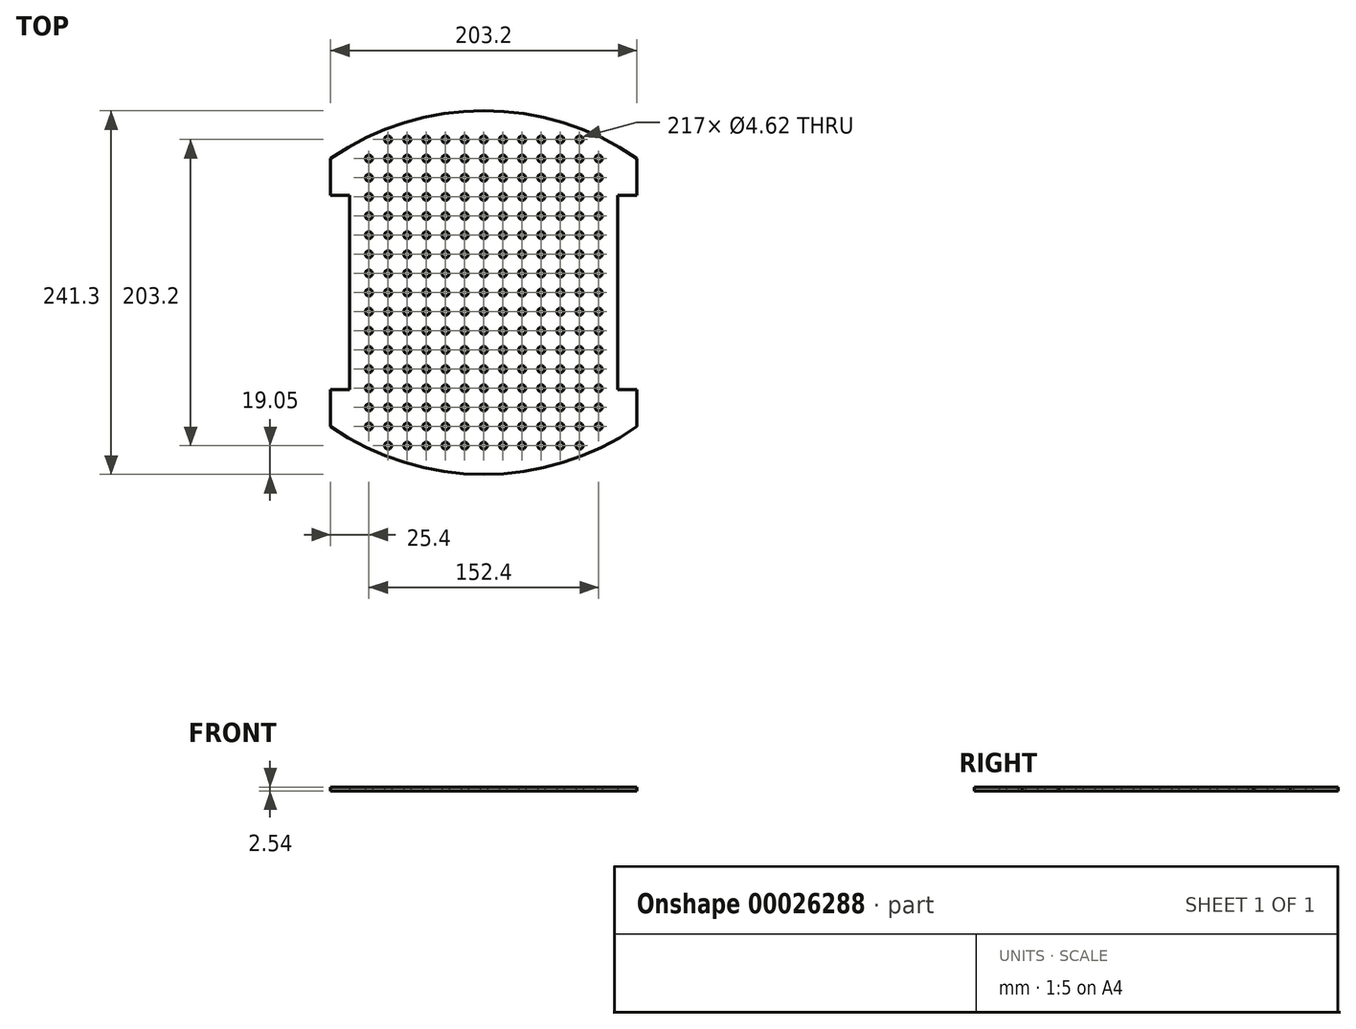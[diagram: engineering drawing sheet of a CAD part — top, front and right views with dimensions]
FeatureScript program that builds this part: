
annotation { "Feature Type Name" : "Feature", "Feature Type Description" : "" }
export const myFeature = defineFeature(function(context is Context, id is Id, definition is map)
    precondition{}
    {
        {
            var Q0;
            Q0=qCreatedBy(makeId("Top.planeOp"),FACE);
            var sketch = newSketch(context, id + "F0", { "sketchPlane" : qUnion([Q0])});
            skLineSegment(sketch, "E0", {"start": v(-101.6, 64.48) * mm, "end": v(-101.6, 88.9) * mm});
            skPoint(sketch, "E1.orphan", {"position": v(0, 120.65) * mm});
            skLineSegment(sketch, "E2.MirrorCS", {"start": v(-101.6, -88.9) * mm, "end": v(-101.6, -64.48) * mm});
            skLineSegment(sketch, "E3.MirrorCS", {"start": v(101.6, -88.9) * mm, "end": v(101.6, -64.48) * mm});
            skLineSegment(sketch, "E4.bottom", {"start": v(-101.6, 64.48) * mm, "end": v(-88.9, 64.48) * mm});
            skLineSegment(sketch, "E4.top", {"start": v(-101.6, -64.48) * mm, "end": v(-88.9, -64.48) * mm});
            skLineSegment(sketch, "E4.right", {"start": v(-88.9, 64.48) * mm, "end": v(-88.9, -64.48) * mm});
            skLineSegment(sketch, "E5.trimOffspring", {"start": v(-101.6, -64.48) * mm, "end": v(-101.6, -83.53) * mm});
            skLineSegment(sketch, "E6.MirrorCS", {"start": v(101.6, 64.48) * mm, "end": v(88.9, 64.48) * mm});
            skLineSegment(sketch, "E7.MirrorCS", {"start": v(88.9, 64.48) * mm, "end": v(88.9, -64.48) * mm});
            skLineSegment(sketch, "E8.MirrorCS", {"start": v(101.6, -64.48) * mm, "end": v(88.9, -64.48) * mm});
            skPoint(sketch, "E9.orphan", {"position": v(101.6, 64.48) * mm});
            skLineSegment(sketch, "E10", {"start": v(101.6, 88.9) * mm, "end": v(101.6, 64.48) * mm});
            skPoint(sketch, "E11.MirrorCS.end.orphan", {"position": v(0, -120.65) * mm});
            skLineSegment(sketch, "E12.trimOffspring", {"start": v(7.61, 0) * mm, "end": v(7.62, 0) * mm, "construction": true});
            skPoint(sketch, "E13.orphan", {"position": v(-101.6, -88.9) * mm});
            skPoint(sketch, "E14.MirrorCS.start.orphan", {"position": v(101.6, -88.9) * mm});
            skArc(sketch, "E15", {"start": v(101.6, 88.9) * mm, "mid": v(0, 120.65) * mm, "end": v(-101.6, 88.9) * mm});
            skArc(sketch, "E16", {"start": v(-101.6, -88.9) * mm, "mid": v(0, -120.65) * mm, "end": v(101.6, -88.9) * mm});
            skCircle(sketch, "E17", {"center": v(0, 0) * mm, "radius": 2.31 * mm});
            skCircle(sketch, "E18.0.1.0", {"center": v(0, 12.7) * mm, "radius": 2.31 * mm});
            skCircle(sketch, "E18.0.2.0", {"center": v(0, 25.4) * mm, "radius": 2.31 * mm});
            skCircle(sketch, "E18.0.3.0", {"center": v(0, 38.1) * mm, "radius": 2.31 * mm});
            skCircle(sketch, "E18.0.4.0", {"center": v(0, 50.8) * mm, "radius": 2.31 * mm});
            skCircle(sketch, "E18.0.5.0", {"center": v(0, 63.5) * mm, "radius": 2.31 * mm});
            skCircle(sketch, "E18.0.6.0", {"center": v(0, 76.2) * mm, "radius": 2.31 * mm});
            skCircle(sketch, "E18.0.7.0", {"center": v(0, 88.9) * mm, "radius": 2.31 * mm});
            skCircle(sketch, "E18.0.8.0", {"center": v(0, 101.6) * mm, "radius": 2.31 * mm});
            skCircle(sketch, "E18.1.0.0", {"center": v(12.7, 0) * mm, "radius": 2.31 * mm});
            skCircle(sketch, "E18.1.1.0", {"center": v(12.7, 12.7) * mm, "radius": 2.31 * mm});
            skCircle(sketch, "E18.1.2.0", {"center": v(12.7, 25.4) * mm, "radius": 2.31 * mm});
            skCircle(sketch, "E18.1.3.0", {"center": v(12.7, 38.1) * mm, "radius": 2.31 * mm});
            skCircle(sketch, "E18.1.4.0", {"center": v(12.7, 50.8) * mm, "radius": 2.31 * mm});
            skCircle(sketch, "E18.1.5.0", {"center": v(12.7, 63.5) * mm, "radius": 2.31 * mm});
            skCircle(sketch, "E18.1.6.0", {"center": v(12.7, 76.2) * mm, "radius": 2.31 * mm});
            skCircle(sketch, "E18.1.7.0", {"center": v(12.7, 88.9) * mm, "radius": 2.31 * mm});
            skCircle(sketch, "E18.1.8.0", {"center": v(12.7, 101.6) * mm, "radius": 2.31 * mm});
            skCircle(sketch, "E18.2.0.0", {"center": v(25.4, 0) * mm, "radius": 2.31 * mm});
            skCircle(sketch, "E18.2.1.0", {"center": v(25.4, 12.7) * mm, "radius": 2.31 * mm});
            skCircle(sketch, "E18.2.2.0", {"center": v(25.4, 25.4) * mm, "radius": 2.31 * mm});
            skCircle(sketch, "E18.2.3.0", {"center": v(25.4, 38.1) * mm, "radius": 2.31 * mm});
            skCircle(sketch, "E18.2.4.0", {"center": v(25.4, 50.8) * mm, "radius": 2.31 * mm});
            skCircle(sketch, "E18.2.5.0", {"center": v(25.4, 63.5) * mm, "radius": 2.31 * mm});
            skCircle(sketch, "E18.2.6.0", {"center": v(25.4, 76.2) * mm, "radius": 2.31 * mm});
            skCircle(sketch, "E18.2.7.0", {"center": v(25.4, 88.9) * mm, "radius": 2.31 * mm});
            skCircle(sketch, "E18.2.8.0", {"center": v(25.4, 101.6) * mm, "radius": 2.31 * mm});
            skCircle(sketch, "E18.3.0.0", {"center": v(38.1, 0) * mm, "radius": 2.31 * mm});
            skCircle(sketch, "E18.3.1.0", {"center": v(38.1, 12.7) * mm, "radius": 2.31 * mm});
            skCircle(sketch, "E18.3.2.0", {"center": v(38.1, 25.4) * mm, "radius": 2.31 * mm});
            skCircle(sketch, "E18.3.3.0", {"center": v(38.1, 38.1) * mm, "radius": 2.31 * mm});
            skCircle(sketch, "E18.3.4.0", {"center": v(38.1, 50.8) * mm, "radius": 2.31 * mm});
            skCircle(sketch, "E18.3.5.0", {"center": v(38.1, 63.5) * mm, "radius": 2.31 * mm});
            skCircle(sketch, "E18.3.6.0", {"center": v(38.1, 76.2) * mm, "radius": 2.31 * mm});
            skCircle(sketch, "E18.3.7.0", {"center": v(38.1, 88.9) * mm, "radius": 2.31 * mm});
            skCircle(sketch, "E18.3.8.0", {"center": v(38.1, 101.6) * mm, "radius": 2.31 * mm});
            skCircle(sketch, "E18.4.0.0", {"center": v(50.8, 0) * mm, "radius": 2.31 * mm});
            skCircle(sketch, "E18.4.1.0", {"center": v(50.8, 12.7) * mm, "radius": 2.31 * mm});
            skCircle(sketch, "E18.4.2.0", {"center": v(50.8, 25.4) * mm, "radius": 2.31 * mm});
            skCircle(sketch, "E18.4.3.0", {"center": v(50.8, 38.1) * mm, "radius": 2.31 * mm});
            skCircle(sketch, "E18.4.4.0", {"center": v(50.8, 50.8) * mm, "radius": 2.31 * mm});
            skCircle(sketch, "E18.4.5.0", {"center": v(50.8, 63.5) * mm, "radius": 2.31 * mm});
            skCircle(sketch, "E18.4.6.0", {"center": v(50.8, 76.2) * mm, "radius": 2.31 * mm});
            skCircle(sketch, "E18.4.7.0", {"center": v(50.8, 88.9) * mm, "radius": 2.31 * mm});
            skCircle(sketch, "E18.4.8.0", {"center": v(50.8, 101.6) * mm, "radius": 2.31 * mm});
            skCircle(sketch, "E18.5.0.0", {"center": v(63.5, 0) * mm, "radius": 2.31 * mm});
            skCircle(sketch, "E18.5.1.0", {"center": v(63.5, 12.7) * mm, "radius": 2.31 * mm});
            skCircle(sketch, "E18.5.2.0", {"center": v(63.5, 25.4) * mm, "radius": 2.31 * mm});
            skCircle(sketch, "E18.5.3.0", {"center": v(63.5, 38.1) * mm, "radius": 2.31 * mm});
            skCircle(sketch, "E18.5.4.0", {"center": v(63.5, 50.8) * mm, "radius": 2.31 * mm});
            skCircle(sketch, "E18.5.5.0", {"center": v(63.5, 63.5) * mm, "radius": 2.31 * mm});
            skCircle(sketch, "E18.5.6.0", {"center": v(63.5, 76.2) * mm, "radius": 2.31 * mm});
            skCircle(sketch, "E18.5.7.0", {"center": v(63.5, 88.9) * mm, "radius": 2.31 * mm});
            skCircle(sketch, "E18.5.8.0", {"center": v(63.5, 101.6) * mm, "radius": 2.31 * mm});
            skCircle(sketch, "E18.6.0.0", {"center": v(76.2, 0) * mm, "radius": 2.31 * mm});
            skCircle(sketch, "E18.6.1.0", {"center": v(76.2, 12.7) * mm, "radius": 2.31 * mm});
            skCircle(sketch, "E18.6.2.0", {"center": v(76.2, 25.4) * mm, "radius": 2.31 * mm});
            skCircle(sketch, "E18.6.3.0", {"center": v(76.2, 38.1) * mm, "radius": 2.31 * mm});
            skCircle(sketch, "E18.6.4.0", {"center": v(76.2, 50.8) * mm, "radius": 2.31 * mm});
            skCircle(sketch, "E18.6.5.0", {"center": v(76.2, 63.5) * mm, "radius": 2.31 * mm});
            skCircle(sketch, "E18.6.6.0", {"center": v(76.2, 76.2) * mm, "radius": 2.31 * mm});
            skCircle(sketch, "E18.6.7.0", {"center": v(76.2, 88.9) * mm, "radius": 2.31 * mm});
            skLineSegment(sketch, "E18.direction1", {"start": v(0, 0) * mm, "end": v(12.7, 0) * mm, "construction": true});
            skLineSegment(sketch, "E18.direction2", {"start": v(0, 0) * mm, "end": v(0, 12.7) * mm, "construction": true});
            skCircle(sketch, "E19.MirrorC", {"center": v(-63.5, 63.5) * mm, "radius": 2.31 * mm});
            skCircle(sketch, "E20.MirrorC", {"center": v(-38.1, 38.1) * mm, "radius": 2.31 * mm});
            skCircle(sketch, "E21.MirrorC", {"center": v(-38.1, 12.7) * mm, "radius": 2.31 * mm});
            skCircle(sketch, "E22.MirrorC", {"center": v(-50.8, 88.9) * mm, "radius": 2.31 * mm});
            skCircle(sketch, "E23.MirrorC", {"center": v(-12.7, 76.2) * mm, "radius": 2.31 * mm});
            skCircle(sketch, "E24.MirrorC", {"center": v(-76.2, 0) * mm, "radius": 2.31 * mm});
            skCircle(sketch, "E25.MirrorC", {"center": v(-63.5, 0) * mm, "radius": 2.31 * mm});
            skCircle(sketch, "E26.MirrorC", {"center": v(-12.7, 25.4) * mm, "radius": 2.31 * mm});
            skCircle(sketch, "E27.MirrorC", {"center": v(-76.2, 50.8) * mm, "radius": 2.31 * mm});
            skCircle(sketch, "E28.MirrorC", {"center": v(-76.2, 63.5) * mm, "radius": 2.31 * mm});
            skCircle(sketch, "E29.MirrorC", {"center": v(-12.7, 38.1) * mm, "radius": 2.31 * mm});
            skCircle(sketch, "E30.MirrorC", {"center": v(-63.5, 25.4) * mm, "radius": 2.31 * mm});
            skCircle(sketch, "E31.MirrorC", {"center": v(-50.8, 0) * mm, "radius": 2.31 * mm});
            skCircle(sketch, "E32.MirrorC", {"center": v(-76.2, 88.9) * mm, "radius": 2.31 * mm});
            skCircle(sketch, "E33.MirrorC", {"center": v(-63.5, 88.9) * mm, "radius": 2.31 * mm});
            skCircle(sketch, "E34.MirrorC", {"center": v(-25.4, 63.5) * mm, "radius": 2.31 * mm});
            skCircle(sketch, "E35.MirrorC", {"center": v(-63.5, 101.6) * mm, "radius": 2.31 * mm});
            skCircle(sketch, "E36.MirrorC", {"center": v(-63.5, 76.2) * mm, "radius": 2.31 * mm});
            skCircle(sketch, "E37.MirrorC", {"center": v(-38.1, 101.6) * mm, "radius": 2.31 * mm});
            skCircle(sketch, "E38.MirrorC", {"center": v(-25.4, 12.7) * mm, "radius": 2.31 * mm});
            skCircle(sketch, "E39.MirrorC", {"center": v(-38.1, 76.2) * mm, "radius": 2.31 * mm});
            skCircle(sketch, "E40.MirrorC", {"center": v(-76.2, 25.4) * mm, "radius": 2.31 * mm});
            skCircle(sketch, "E41.MirrorC", {"center": v(-38.1, 0) * mm, "radius": 2.31 * mm});
            skCircle(sketch, "E42.MirrorC", {"center": v(-50.8, 38.1) * mm, "radius": 2.31 * mm});
            skCircle(sketch, "E43.MirrorC", {"center": v(-12.7, 88.9) * mm, "radius": 2.31 * mm});
            skCircle(sketch, "E44.MirrorC", {"center": v(-50.8, 101.6) * mm, "radius": 2.31 * mm});
            skCircle(sketch, "E45.MirrorC", {"center": v(-38.1, 25.4) * mm, "radius": 2.31 * mm});
            skCircle(sketch, "E46.MirrorC", {"center": v(-63.5, 38.1) * mm, "radius": 2.31 * mm});
            skCircle(sketch, "E47.MirrorC", {"center": v(-50.8, 63.5) * mm, "radius": 2.31 * mm});
            skCircle(sketch, "E48.MirrorC", {"center": v(-12.7, 0) * mm, "radius": 2.31 * mm});
            skCircle(sketch, "E49.MirrorC", {"center": v(-25.4, 88.9) * mm, "radius": 2.31 * mm});
            skCircle(sketch, "E50.MirrorC", {"center": v(-38.1, 63.5) * mm, "radius": 2.31 * mm});
            skCircle(sketch, "E51.MirrorC", {"center": v(-76.2, 38.1) * mm, "radius": 2.31 * mm});
            skCircle(sketch, "E52.MirrorC", {"center": v(-12.7, 50.8) * mm, "radius": 2.31 * mm});
            skCircle(sketch, "E53.MirrorC", {"center": v(-76.2, 76.2) * mm, "radius": 2.31 * mm});
            skCircle(sketch, "E54.MirrorC", {"center": v(-12.7, 101.6) * mm, "radius": 2.31 * mm});
            skCircle(sketch, "E55.MirrorC", {"center": v(-50.8, 50.8) * mm, "radius": 2.31 * mm});
            skCircle(sketch, "E56.MirrorC", {"center": v(-50.8, 25.4) * mm, "radius": 2.31 * mm});
            skCircle(sketch, "E57.MirrorC", {"center": v(-63.5, 50.8) * mm, "radius": 2.31 * mm});
            skCircle(sketch, "E58.MirrorC", {"center": v(-25.4, 50.8) * mm, "radius": 2.31 * mm});
            skCircle(sketch, "E59.MirrorC", {"center": v(-63.5, 12.7) * mm, "radius": 2.31 * mm});
            skCircle(sketch, "E60.MirrorC", {"center": v(-38.1, 88.9) * mm, "radius": 2.31 * mm});
            skCircle(sketch, "E61.MirrorC", {"center": v(-25.4, 0) * mm, "radius": 2.31 * mm});
            skCircle(sketch, "E62.MirrorC", {"center": v(-12.7, 63.5) * mm, "radius": 2.31 * mm});
            skCircle(sketch, "E63.MirrorC", {"center": v(-50.8, 76.2) * mm, "radius": 2.31 * mm});
            skCircle(sketch, "E64.MirrorC", {"center": v(-25.4, 101.6) * mm, "radius": 2.31 * mm});
            skCircle(sketch, "E65.MirrorC", {"center": v(-12.7, 12.7) * mm, "radius": 2.31 * mm});
            skCircle(sketch, "E66.MirrorC", {"center": v(-38.1, 50.8) * mm, "radius": 2.31 * mm});
            skCircle(sketch, "E67.MirrorC", {"center": v(-25.4, 76.2) * mm, "radius": 2.31 * mm});
            skCircle(sketch, "E68.MirrorC", {"center": v(-76.2, 12.7) * mm, "radius": 2.31 * mm});
            skCircle(sketch, "E69.MirrorC", {"center": v(-25.4, 25.4) * mm, "radius": 2.31 * mm});
            skCircle(sketch, "E70.MirrorC", {"center": v(-25.4, 38.1) * mm, "radius": 2.31 * mm});
            skCircle(sketch, "E71.MirrorC", {"center": v(-50.8, 12.7) * mm, "radius": 2.31 * mm});
            skCircle(sketch, "E72.MirrorC", {"center": v(0, -12.7) * mm, "radius": 2.31 * mm});
            skCircle(sketch, "E73.MirrorC", {"center": v(63.5, -63.5) * mm, "radius": 2.31 * mm});
            skCircle(sketch, "E74.MirrorC", {"center": v(76.2, -38.1) * mm, "radius": 2.31 * mm});
            skCircle(sketch, "E75.MirrorC", {"center": v(-50.8, -76.2) * mm, "radius": 2.31 * mm});
            skCircle(sketch, "E76.MirrorC", {"center": v(0, -63.5) * mm, "radius": 2.31 * mm});
            skCircle(sketch, "E77.MirrorC", {"center": v(12.7, -38.1) * mm, "radius": 2.31 * mm});
            skCircle(sketch, "E78.MirrorC", {"center": v(63.5, -12.7) * mm, "radius": 2.31 * mm});
            skCircle(sketch, "E79.MirrorC", {"center": v(-50.8, -25.4) * mm, "radius": 2.31 * mm});
            skCircle(sketch, "E80.MirrorC", {"center": v(-50.8, -101.6) * mm, "radius": 2.31 * mm});
            skCircle(sketch, "E81.MirrorC", {"center": v(-76.2, -12.7) * mm, "radius": 2.31 * mm});
            skCircle(sketch, "E82.MirrorC", {"center": v(-38.1, -38.1) * mm, "radius": 2.31 * mm});
            skCircle(sketch, "E83.MirrorC", {"center": v(-63.5, -38.1) * mm, "radius": 2.31 * mm});
            skCircle(sketch, "E84.MirrorC", {"center": v(-38.1, -101.6) * mm, "radius": 2.31 * mm});
            skCircle(sketch, "E85.MirrorC", {"center": v(50.8, -12.7) * mm, "radius": 2.31 * mm});
            skCircle(sketch, "E86.MirrorC", {"center": v(-12.7, -25.4) * mm, "radius": 2.31 * mm});
            skCircle(sketch, "E87.MirrorC", {"center": v(76.2, -12.7) * mm, "radius": 2.31 * mm});
            skCircle(sketch, "E88.MirrorC", {"center": v(-50.8, -88.9) * mm, "radius": 2.31 * mm});
            skCircle(sketch, "E89.MirrorC", {"center": v(25.4, -63.5) * mm, "radius": 2.31 * mm});
            skCircle(sketch, "E90.MirrorC", {"center": v(63.5, -76.2) * mm, "radius": 2.31 * mm});
            skCircle(sketch, "E91.MirrorC", {"center": v(38.1, -38.1) * mm, "radius": 2.31 * mm});
            skCircle(sketch, "E92.MirrorC", {"center": v(25.4, -12.7) * mm, "radius": 2.31 * mm});
            skCircle(sketch, "E93.MirrorC", {"center": v(0, -101.6) * mm, "radius": 2.31 * mm});
            skCircle(sketch, "E94.MirrorC", {"center": v(25.4, -76.2) * mm, "radius": 2.31 * mm});
            skCircle(sketch, "E95.MirrorC", {"center": v(12.7, -12.7) * mm, "radius": 2.31 * mm});
            skCircle(sketch, "E96.MirrorC", {"center": v(-25.4, -63.5) * mm, "radius": 2.31 * mm});
            skCircle(sketch, "E97.MirrorC", {"center": v(-25.4, -38.1) * mm, "radius": 2.31 * mm});
            skCircle(sketch, "E98.MirrorC", {"center": v(-25.4, -12.7) * mm, "radius": 2.31 * mm});
            skCircle(sketch, "E99.MirrorC", {"center": v(0, -38.1) * mm, "radius": 2.31 * mm});
            skCircle(sketch, "E100.MirrorC", {"center": v(-12.7, -50.8) * mm, "radius": 2.31 * mm});
            skCircle(sketch, "E101.MirrorC", {"center": v(50.8, -88.9) * mm, "radius": 2.31 * mm});
            skCircle(sketch, "E102.MirrorC", {"center": v(12.7, -101.6) * mm, "radius": 2.31 * mm});
            skCircle(sketch, "E103.MirrorC", {"center": v(63.5, -25.4) * mm, "radius": 2.31 * mm});
            skCircle(sketch, "E104.MirrorC", {"center": v(76.2, -88.9) * mm, "radius": 2.31 * mm});
            skCircle(sketch, "E105.MirrorC", {"center": v(50.8, -63.5) * mm, "radius": 2.31 * mm});
            skCircle(sketch, "E106.MirrorC", {"center": v(0, -88.9) * mm, "radius": 2.31 * mm});
            skCircle(sketch, "E107.MirrorC", {"center": v(25.4, -88.9) * mm, "radius": 2.31 * mm});
            skCircle(sketch, "E108.MirrorC", {"center": v(0, -76.2) * mm, "radius": 2.31 * mm});
            skCircle(sketch, "E109.MirrorC", {"center": v(63.5, -88.9) * mm, "radius": 2.31 * mm});
            skCircle(sketch, "E110.MirrorC", {"center": v(-50.8, -38.1) * mm, "radius": 2.31 * mm});
            skCircle(sketch, "E111.MirrorC", {"center": v(-38.1, -25.4) * mm, "radius": 2.31 * mm});
            skCircle(sketch, "E112.MirrorC", {"center": v(76.2, -25.4) * mm, "radius": 2.31 * mm});
            skCircle(sketch, "E113.MirrorC", {"center": v(50.8, -76.2) * mm, "radius": 2.31 * mm});
            skCircle(sketch, "E114.MirrorC", {"center": v(25.4, -101.6) * mm, "radius": 2.31 * mm});
            skCircle(sketch, "E115.MirrorC", {"center": v(12.7, -76.2) * mm, "radius": 2.31 * mm});
            skCircle(sketch, "E116.MirrorC", {"center": v(-76.2, -88.9) * mm, "radius": 2.31 * mm});
            skCircle(sketch, "E117.MirrorC", {"center": v(-38.1, -63.5) * mm, "radius": 2.31 * mm});
            skCircle(sketch, "E118.MirrorC", {"center": v(-63.5, -12.7) * mm, "radius": 2.31 * mm});
            skCircle(sketch, "E119.MirrorC", {"center": v(-38.1, -12.7) * mm, "radius": 2.31 * mm});
            skCircle(sketch, "E120.MirrorC", {"center": v(76.2, -76.2) * mm, "radius": 2.31 * mm});
            skCircle(sketch, "E121.MirrorC", {"center": v(25.4, -25.4) * mm, "radius": 2.31 * mm});
            skCircle(sketch, "E122.MirrorC", {"center": v(0, -25.4) * mm, "radius": 2.31 * mm});
            skCircle(sketch, "E123.MirrorC", {"center": v(-76.2, -76.2) * mm, "radius": 2.31 * mm});
            skCircle(sketch, "E124.MirrorC", {"center": v(-50.8, -63.5) * mm, "radius": 2.31 * mm});
            skCircle(sketch, "E125.MirrorC", {"center": v(-25.4, -25.4) * mm, "radius": 2.31 * mm});
            skCircle(sketch, "E126.MirrorC", {"center": v(-50.8, -12.7) * mm, "radius": 2.31 * mm});
            skCircle(sketch, "E127.MirrorC", {"center": v(-76.2, -63.5) * mm, "radius": 2.31 * mm});
            skCircle(sketch, "E128.MirrorC", {"center": v(-38.1, -76.2) * mm, "radius": 2.31 * mm});
            skCircle(sketch, "E129.MirrorC", {"center": v(38.1, -12.7) * mm, "radius": 2.31 * mm});
            skCircle(sketch, "E130.MirrorC", {"center": v(-38.1, -88.9) * mm, "radius": 2.31 * mm});
            skCircle(sketch, "E131.MirrorC", {"center": v(-76.2, -38.1) * mm, "radius": 2.31 * mm});
            skCircle(sketch, "E132.MirrorC", {"center": v(-25.4, -76.2) * mm, "radius": 2.31 * mm});
            skCircle(sketch, "E133.MirrorC", {"center": v(-25.4, -88.9) * mm, "radius": 2.31 * mm});
            skCircle(sketch, "E134.MirrorC", {"center": v(50.8, -38.1) * mm, "radius": 2.31 * mm});
            skCircle(sketch, "E135.MirrorC", {"center": v(25.4, -38.1) * mm, "radius": 2.31 * mm});
            skCircle(sketch, "E136.MirrorC", {"center": v(-76.2, -25.4) * mm, "radius": 2.31 * mm});
            skCircle(sketch, "E137.MirrorC", {"center": v(12.7, -88.9) * mm, "radius": 2.31 * mm});
            skCircle(sketch, "E138.MirrorC", {"center": v(12.7, -63.5) * mm, "radius": 2.31 * mm});
            skCircle(sketch, "E139.MirrorC", {"center": v(63.5, -38.1) * mm, "radius": 2.31 * mm});
            skCircle(sketch, "E140.MirrorC", {"center": v(76.2, -63.5) * mm, "radius": 2.31 * mm});
            skCircle(sketch, "E141.MirrorC", {"center": v(12.7, -25.4) * mm, "radius": 2.31 * mm});
            skCircle(sketch, "E142.MirrorC", {"center": v(50.8, -25.4) * mm, "radius": 2.31 * mm});
            skCircle(sketch, "E143.MirrorC", {"center": v(38.1, -25.4) * mm, "radius": 2.31 * mm});
            skCircle(sketch, "E144.MirrorC", {"center": v(-63.5, -88.9) * mm, "radius": 2.31 * mm});
            skCircle(sketch, "E145.MirrorC", {"center": v(76.2, -50.8) * mm, "radius": 2.31 * mm});
            skCircle(sketch, "E146.MirrorC", {"center": v(-63.5, -76.2) * mm, "radius": 2.31 * mm});
            skCircle(sketch, "E147.MirrorC", {"center": v(38.1, -76.2) * mm, "radius": 2.31 * mm});
            skCircle(sketch, "E148.MirrorC", {"center": v(12.7, -50.8) * mm, "radius": 2.31 * mm});
            skCircle(sketch, "E149.MirrorC", {"center": v(63.5, -101.6) * mm, "radius": 2.31 * mm});
            skCircle(sketch, "E150.MirrorC", {"center": v(-25.4, -50.8) * mm, "radius": 2.31 * mm});
            skCircle(sketch, "E151.MirrorC", {"center": v(-63.5, -63.5) * mm, "radius": 2.31 * mm});
            skCircle(sketch, "E152.MirrorC", {"center": v(38.1, -101.6) * mm, "radius": 2.31 * mm});
            skCircle(sketch, "E153.MirrorC", {"center": v(-76.2, -50.8) * mm, "radius": 2.31 * mm});
            skCircle(sketch, "E154.MirrorC", {"center": v(-12.7, -101.6) * mm, "radius": 2.31 * mm});
            skCircle(sketch, "E155.MirrorC", {"center": v(-12.7, -38.1) * mm, "radius": 2.31 * mm});
            skCircle(sketch, "E156.MirrorC", {"center": v(63.5, -50.8) * mm, "radius": 2.31 * mm});
            skCircle(sketch, "E157.MirrorC", {"center": v(-12.7, -63.5) * mm, "radius": 2.31 * mm});
            skCircle(sketch, "E158.MirrorC", {"center": v(0, -50.8) * mm, "radius": 2.31 * mm});
            skCircle(sketch, "E159.MirrorC", {"center": v(-12.7, -12.7) * mm, "radius": 2.31 * mm});
            skCircle(sketch, "E160.MirrorC", {"center": v(-12.7, -76.2) * mm, "radius": 2.31 * mm});
            skCircle(sketch, "E161.MirrorC", {"center": v(38.1, -88.9) * mm, "radius": 2.31 * mm});
            skCircle(sketch, "E162.MirrorC", {"center": v(50.8, -50.8) * mm, "radius": 2.31 * mm});
            skCircle(sketch, "E163.MirrorC", {"center": v(-12.7, -88.9) * mm, "radius": 2.31 * mm});
            skCircle(sketch, "E164.MirrorC", {"center": v(38.1, -50.8) * mm, "radius": 2.31 * mm});
            skCircle(sketch, "E165.MirrorC", {"center": v(-50.8, -50.8) * mm, "radius": 2.31 * mm});
            skCircle(sketch, "E166.MirrorC", {"center": v(50.8, -101.6) * mm, "radius": 2.31 * mm});
            skCircle(sketch, "E167.MirrorC", {"center": v(-25.4, -101.6) * mm, "radius": 2.31 * mm});
            skCircle(sketch, "E168.MirrorC", {"center": v(-63.5, -101.6) * mm, "radius": 2.31 * mm});
            skCircle(sketch, "E169.MirrorC", {"center": v(38.1, -63.5) * mm, "radius": 2.31 * mm});
            skCircle(sketch, "E170.MirrorC", {"center": v(-63.5, -25.4) * mm, "radius": 2.31 * mm});
            skCircle(sketch, "E171.MirrorC", {"center": v(-38.1, -50.8) * mm, "radius": 2.31 * mm});
            skCircle(sketch, "E172.MirrorC", {"center": v(-63.5, -50.8) * mm, "radius": 2.31 * mm});
            skCircle(sketch, "E173.MirrorC", {"center": v(25.4, -50.8) * mm, "radius": 2.31 * mm});
            skLineSegment(sketch, "E174", {"start": v(-76.2, 0) * mm, "end": v(-88.9, 0) * mm});
            skSolve(sketch);
        }
        {
            var Q0;
            Q0=makeQuery(id+"F0.imprint","IMPRINT",FACE,{"disambiguationData":[TD([[makeQuery(id+"F0.imprint","IMPRINT",EDGE,{"derivedFrom":sQuery(id+"F0.wireOp",EDGE,"E0")}),-1.0]])]});
            extrude(context, id + "F1", {"entities" : qUnion([Q0]), "depth" : 2.54 * mm});
        }
    });
